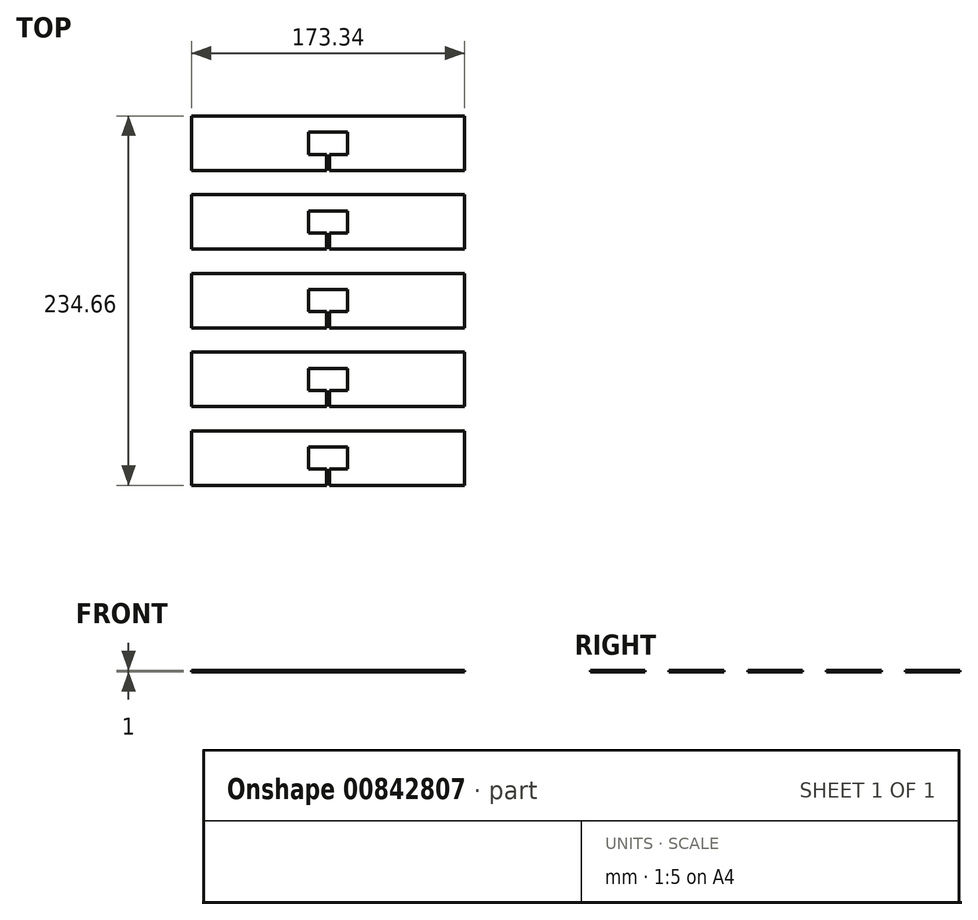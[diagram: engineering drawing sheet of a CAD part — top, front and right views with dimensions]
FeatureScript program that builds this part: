
annotation { "Feature Type Name" : "Feature", "Feature Type Description" : "" }
export const myFeature = defineFeature(function(context is Context, id is Id, definition is map)
    precondition{}
    {
        {
            var Q0;
            Q0=qCreatedBy(makeId("Top.planeOp"),FACE);
            var sketch = newSketch(context, id + "F0", { "sketchPlane" : qUnion([Q0])});
            skLineSegment(sketch, "E0", {"start": v(0, 17.33) * mm, "end": v(86.67, 17.33) * mm});
            skLineSegment(sketch, "E1", {"start": v(86.67, 17.33) * mm, "end": v(86.67, 0) * mm});
            skLineSegment(sketch, "E2", {"start": v(0, 7.04) * mm, "end": v(12.4, 7.04) * mm});
            skLineSegment(sketch, "E3", {"start": v(12.4, 7.04) * mm, "end": v(12.4, 0) * mm});
            skLineSegment(sketch, "E4.MirrorCS", {"start": v(0, 17.33) * mm, "end": v(-86.67, 17.33) * mm});
            skLineSegment(sketch, "E5.MirrorCS", {"start": v(-86.67, 17.33) * mm, "end": v(-86.67, 0) * mm});
            skLineSegment(sketch, "E6.MirrorCS", {"start": v(0, 7.04) * mm, "end": v(-12.4, 7.04) * mm});
            skLineSegment(sketch, "E7.MirrorCS", {"start": v(-12.4, 7.04) * mm, "end": v(-12.4, 0) * mm});
            skLineSegment(sketch, "E8.MirrorCS", {"start": v(-1, -7.04) * mm, "end": v(-12.4, -7.04) * mm});
            skLineSegment(sketch, "E9.MirrorCS", {"start": v(1, -7.04) * mm, "end": v(12.4, -7.04) * mm});
            skLineSegment(sketch, "E10.MirrorCS", {"start": v(1, -17.33) * mm, "end": v(86.67, -17.33) * mm});
            skLineSegment(sketch, "E11.MirrorCS", {"start": v(-1, -17.33) * mm, "end": v(-86.67, -17.33) * mm});
            skLineSegment(sketch, "E12.MirrorCS", {"start": v(-86.67, -17.33) * mm, "end": v(-86.67, 0) * mm});
            skLineSegment(sketch, "E13.MirrorCS", {"start": v(86.67, -17.33) * mm, "end": v(86.67, 0) * mm});
            skLineSegment(sketch, "E14.MirrorCS", {"start": v(-12.4, -7.04) * mm, "end": v(-12.4, 0) * mm});
            skLineSegment(sketch, "E15.MirrorCS", {"start": v(12.4, -7.04) * mm, "end": v(12.4, 0) * mm});
            skLineSegment(sketch, "E16", {"start": v(-1, -7.04) * mm, "end": v(-1, -17.33) * mm});
            skLineSegment(sketch, "E17.MirrorCS", {"start": v(1, -7.04) * mm, "end": v(1, -17.33) * mm});
            skPoint(sketch, "E18.orphan", {"position": v(0, -7.04) * mm});
            skPoint(sketch, "E19.orphan", {"position": v(0, -17.33) * mm});
            skLineSegment(sketch, "E20.0.1.0", {"start": v(86.67, 67.33) * mm, "end": v(86.67, 50) * mm});
            skLineSegment(sketch, "E20.0.1.1", {"start": v(-86.67, 67.33) * mm, "end": v(-86.67, 50) * mm});
            skLineSegment(sketch, "E20.0.1.2", {"start": v(0, 67.33) * mm, "end": v(86.67, 67.33) * mm});
            skPoint(sketch, "E20.0.1.3", {"position": v(0, 42.96) * mm});
            skLineSegment(sketch, "E20.0.1.4", {"start": v(-86.67, 32.67) * mm, "end": v(-86.67, 50) * mm});
            skLineSegment(sketch, "E20.0.1.5", {"start": v(0, 57.04) * mm, "end": v(-12.4, 57.04) * mm});
            skLineSegment(sketch, "E20.0.1.6", {"start": v(0, 67.33) * mm, "end": v(-86.67, 67.33) * mm});
            skLineSegment(sketch, "E20.0.1.7", {"start": v(0, 57.04) * mm, "end": v(12.4, 57.04) * mm});
            skLineSegment(sketch, "E20.0.1.8", {"start": v(-1, 42.96) * mm, "end": v(-12.4, 42.96) * mm});
            skLineSegment(sketch, "E20.0.1.9", {"start": v(1, 32.67) * mm, "end": v(86.67, 32.67) * mm});
            skLineSegment(sketch, "E20.0.1.10", {"start": v(1, 42.96) * mm, "end": v(12.4, 42.96) * mm});
            skLineSegment(sketch, "E20.0.1.11", {"start": v(-1, 32.67) * mm, "end": v(-86.67, 32.67) * mm});
            skPoint(sketch, "E20.0.1.12", {"position": v(0, 32.67) * mm});
            skLineSegment(sketch, "E20.0.1.13", {"start": v(86.67, 32.67) * mm, "end": v(86.67, 50) * mm});
            skPoint(sketch, "E20.0.1.14", {"position": v(0, 32.67) * mm});
            skPoint(sketch, "E20.0.1.15", {"position": v(0, 42.96) * mm});
            skLineSegment(sketch, "E20.0.1.16", {"start": v(-1, 42.96) * mm, "end": v(-1, 32.67) * mm});
            skLineSegment(sketch, "E20.0.1.17", {"start": v(12.4, 42.96) * mm, "end": v(12.4, 50) * mm});
            skLineSegment(sketch, "E20.0.1.18", {"start": v(-12.4, 57.04) * mm, "end": v(-12.4, 50) * mm});
            skLineSegment(sketch, "E20.0.1.19", {"start": v(1, 42.96) * mm, "end": v(1, 32.67) * mm});
            skLineSegment(sketch, "E20.0.1.20", {"start": v(12.4, 57.04) * mm, "end": v(12.4, 50) * mm});
            skLineSegment(sketch, "E20.0.1.21", {"start": v(-12.4, 42.96) * mm, "end": v(-12.4, 50) * mm});
            skLineSegment(sketch, "E20.0.2.0", {"start": v(86.67, 117.33) * mm, "end": v(86.67, 100) * mm});
            skLineSegment(sketch, "E20.0.2.1", {"start": v(-86.67, 117.33) * mm, "end": v(-86.67, 100) * mm});
            skLineSegment(sketch, "E20.0.2.2", {"start": v(0, 117.33) * mm, "end": v(86.67, 117.33) * mm});
            skPoint(sketch, "E20.0.2.3", {"position": v(0, 92.96) * mm});
            skLineSegment(sketch, "E20.0.2.4", {"start": v(-86.67, 82.67) * mm, "end": v(-86.67, 100) * mm});
            skLineSegment(sketch, "E20.0.2.5", {"start": v(0, 107.04) * mm, "end": v(-12.4, 107.04) * mm});
            skLineSegment(sketch, "E20.0.2.6", {"start": v(0, 117.33) * mm, "end": v(-86.67, 117.33) * mm});
            skLineSegment(sketch, "E20.0.2.7", {"start": v(0, 107.04) * mm, "end": v(12.4, 107.04) * mm});
            skLineSegment(sketch, "E20.0.2.8", {"start": v(-1, 92.96) * mm, "end": v(-12.4, 92.96) * mm});
            skLineSegment(sketch, "E20.0.2.9", {"start": v(1, 82.67) * mm, "end": v(86.67, 82.67) * mm});
            skLineSegment(sketch, "E20.0.2.10", {"start": v(1, 92.96) * mm, "end": v(12.4, 92.96) * mm});
            skLineSegment(sketch, "E20.0.2.11", {"start": v(-1, 82.67) * mm, "end": v(-86.67, 82.67) * mm});
            skPoint(sketch, "E20.0.2.12", {"position": v(0, 82.67) * mm});
            skLineSegment(sketch, "E20.0.2.13", {"start": v(86.67, 82.67) * mm, "end": v(86.67, 100) * mm});
            skPoint(sketch, "E20.0.2.14", {"position": v(0, 82.67) * mm});
            skPoint(sketch, "E20.0.2.15", {"position": v(0, 92.96) * mm});
            skLineSegment(sketch, "E20.0.2.16", {"start": v(-1, 92.96) * mm, "end": v(-1, 82.67) * mm});
            skLineSegment(sketch, "E20.0.2.17", {"start": v(12.4, 92.96) * mm, "end": v(12.4, 100) * mm});
            skLineSegment(sketch, "E20.0.2.18", {"start": v(-12.4, 107.04) * mm, "end": v(-12.4, 100) * mm});
            skLineSegment(sketch, "E20.0.2.19", {"start": v(1, 92.96) * mm, "end": v(1, 82.67) * mm});
            skLineSegment(sketch, "E20.0.2.20", {"start": v(12.4, 107.04) * mm, "end": v(12.4, 100) * mm});
            skLineSegment(sketch, "E20.0.2.21", {"start": v(-12.4, 92.96) * mm, "end": v(-12.4, 100) * mm});
            skLineSegment(sketch, "E20.0.3.0", {"start": v(86.67, 167.33) * mm, "end": v(86.67, 150) * mm});
            skLineSegment(sketch, "E20.0.3.1", {"start": v(-86.67, 167.33) * mm, "end": v(-86.67, 150) * mm});
            skLineSegment(sketch, "E20.0.3.2", {"start": v(0, 167.33) * mm, "end": v(86.67, 167.33) * mm});
            skPoint(sketch, "E20.0.3.3", {"position": v(0, 142.96) * mm});
            skLineSegment(sketch, "E20.0.3.4", {"start": v(-86.67, 132.67) * mm, "end": v(-86.67, 150) * mm});
            skLineSegment(sketch, "E20.0.3.5", {"start": v(0, 157.04) * mm, "end": v(-12.4, 157.04) * mm});
            skLineSegment(sketch, "E20.0.3.6", {"start": v(0, 167.33) * mm, "end": v(-86.67, 167.33) * mm});
            skLineSegment(sketch, "E20.0.3.7", {"start": v(0, 157.04) * mm, "end": v(12.4, 157.04) * mm});
            skLineSegment(sketch, "E20.0.3.8", {"start": v(-1, 142.96) * mm, "end": v(-12.4, 142.96) * mm});
            skLineSegment(sketch, "E20.0.3.9", {"start": v(1, 132.67) * mm, "end": v(86.67, 132.67) * mm});
            skLineSegment(sketch, "E20.0.3.10", {"start": v(1, 142.96) * mm, "end": v(12.4, 142.96) * mm});
            skLineSegment(sketch, "E20.0.3.11", {"start": v(-1, 132.67) * mm, "end": v(-86.67, 132.67) * mm});
            skPoint(sketch, "E20.0.3.12", {"position": v(0, 132.67) * mm});
            skLineSegment(sketch, "E20.0.3.13", {"start": v(86.67, 132.67) * mm, "end": v(86.67, 150) * mm});
            skPoint(sketch, "E20.0.3.14", {"position": v(0, 132.67) * mm});
            skPoint(sketch, "E20.0.3.15", {"position": v(0, 142.96) * mm});
            skLineSegment(sketch, "E20.0.3.16", {"start": v(-1, 142.96) * mm, "end": v(-1, 132.67) * mm});
            skLineSegment(sketch, "E20.0.3.17", {"start": v(12.4, 142.96) * mm, "end": v(12.4, 150) * mm});
            skLineSegment(sketch, "E20.0.3.18", {"start": v(-12.4, 157.04) * mm, "end": v(-12.4, 150) * mm});
            skLineSegment(sketch, "E20.0.3.19", {"start": v(1, 142.96) * mm, "end": v(1, 132.67) * mm});
            skLineSegment(sketch, "E20.0.3.20", {"start": v(12.4, 157.04) * mm, "end": v(12.4, 150) * mm});
            skLineSegment(sketch, "E20.0.3.21", {"start": v(-12.4, 142.96) * mm, "end": v(-12.4, 150) * mm});
            skLineSegment(sketch, "E20.0.4.0", {"start": v(86.67, 217.33) * mm, "end": v(86.67, 200) * mm});
            skLineSegment(sketch, "E20.0.4.1", {"start": v(-86.67, 217.33) * mm, "end": v(-86.67, 200) * mm});
            skLineSegment(sketch, "E20.0.4.2", {"start": v(0, 217.33) * mm, "end": v(86.67, 217.33) * mm});
            skPoint(sketch, "E20.0.4.3", {"position": v(0, 192.96) * mm});
            skLineSegment(sketch, "E20.0.4.4", {"start": v(-86.67, 182.67) * mm, "end": v(-86.67, 200) * mm});
            skLineSegment(sketch, "E20.0.4.5", {"start": v(0, 207.04) * mm, "end": v(-12.4, 207.04) * mm});
            skLineSegment(sketch, "E20.0.4.6", {"start": v(0, 217.33) * mm, "end": v(-86.67, 217.33) * mm});
            skLineSegment(sketch, "E20.0.4.7", {"start": v(0, 207.04) * mm, "end": v(12.4, 207.04) * mm});
            skLineSegment(sketch, "E20.0.4.8", {"start": v(-1, 192.96) * mm, "end": v(-12.4, 192.96) * mm});
            skLineSegment(sketch, "E20.0.4.9", {"start": v(1, 182.67) * mm, "end": v(86.67, 182.67) * mm});
            skLineSegment(sketch, "E20.0.4.10", {"start": v(1, 192.96) * mm, "end": v(12.4, 192.96) * mm});
            skLineSegment(sketch, "E20.0.4.11", {"start": v(-1, 182.67) * mm, "end": v(-86.67, 182.67) * mm});
            skPoint(sketch, "E20.0.4.12", {"position": v(0, 182.67) * mm});
            skLineSegment(sketch, "E20.0.4.13", {"start": v(86.67, 182.67) * mm, "end": v(86.67, 200) * mm});
            skPoint(sketch, "E20.0.4.14", {"position": v(0, 182.67) * mm});
            skPoint(sketch, "E20.0.4.15", {"position": v(0, 192.96) * mm});
            skLineSegment(sketch, "E20.0.4.16", {"start": v(-1, 192.96) * mm, "end": v(-1, 182.67) * mm});
            skLineSegment(sketch, "E20.0.4.17", {"start": v(12.4, 192.96) * mm, "end": v(12.4, 200) * mm});
            skLineSegment(sketch, "E20.0.4.18", {"start": v(-12.4, 207.04) * mm, "end": v(-12.4, 200) * mm});
            skLineSegment(sketch, "E20.0.4.19", {"start": v(1, 192.96) * mm, "end": v(1, 182.67) * mm});
            skLineSegment(sketch, "E20.0.4.20", {"start": v(12.4, 207.04) * mm, "end": v(12.4, 200) * mm});
            skLineSegment(sketch, "E20.0.4.21", {"start": v(-12.4, 192.96) * mm, "end": v(-12.4, 200) * mm});
            skLineSegment(sketch, "E20.direction1", {"start": v(-86.67, -17.33) * mm, "end": v(-25, -17.33) * mm, "construction": true});
            skLineSegment(sketch, "E20.direction2", {"start": v(-86.67, -17.33) * mm, "end": v(-86.67, 32.67) * mm, "construction": true});
            skSolve(sketch);
        }
        {
            var Q0;
            Q0=qSketchRegion(id+"F0",true);
            extrude(context, id + "F1", {"entities" : qUnion([Q0]), "depth" : 1 * mm, "offsetDistance" : 25 * mm});
        }
    });
